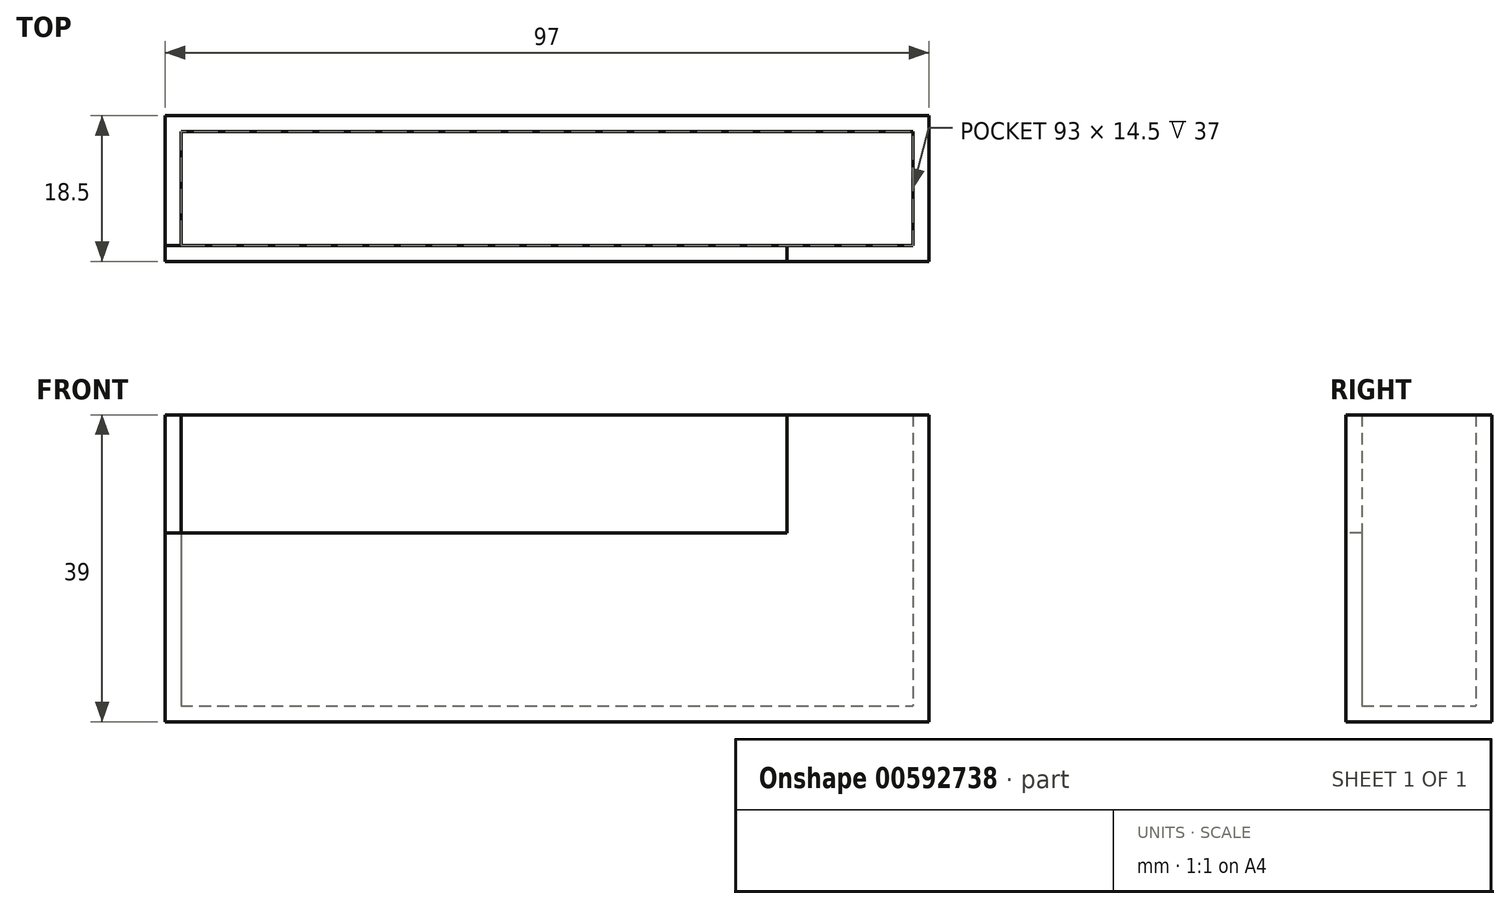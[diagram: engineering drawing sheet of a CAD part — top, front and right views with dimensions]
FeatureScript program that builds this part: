
annotation { "Feature Type Name" : "Feature", "Feature Type Description" : "" }
export const myFeature = defineFeature(function(context is Context, id is Id, definition is map)
    precondition{}
    {
        {
            var Q0;
            Q0=qCreatedBy(makeId("Top.planeOp"),FACE);
            var sketch = newSketch(context, id + "F0", { "sketchPlane" : qUnion([Q0])});
            skLineSegment(sketch, "E0.bottom", {"start": v(0, 0) * mm, "end": v(97, 0) * mm});
            skLineSegment(sketch, "E0.top", {"start": v(0, 18.5) * mm, "end": v(97, 18.5) * mm});
            skLineSegment(sketch, "E0.left", {"start": v(0, 0) * mm, "end": v(0, 18.5) * mm});
            skLineSegment(sketch, "E0.right", {"start": v(97, 0) * mm, "end": v(97, 18.5) * mm});
            skSolve(sketch);
        }
        {
            var Q0;
            Q0 = qSketchRegion(id + "F0", true);
            extrude(context, id + "F1", {"entities" : qUnion([Q0]), "depth" : 2 * mm, "offsetDistance" : 25 * mm});
        }
        {
            var Q0;
            Q0=makeQuery(id+"F1.opExtrude","CAP_FACE",FACE,{"disambiguationData":[OSD([sQuery(id+"F0.wireOp",EDGE,"E0.bottom"),sQuery(id+"F0.wireOp",EDGE,"E0.top"),sQuery(id+"F0.wireOp",EDGE,"E0.left"),sQuery(id+"F0.wireOp",EDGE,"E0.right")])],"isStart":false});
            var sketch = newSketch(context, id + "F2", { "sketchPlane" : qUnion([Q0])});
            skLineSegment(sketch, "E1.bottom", {"start": v(0, 0) * mm, "end": v(2, 0) * mm});
            skLineSegment(sketch, "E1.top", {"start": v(0, 2) * mm, "end": v(2, 2) * mm});
            skLineSegment(sketch, "E1.left", {"start": v(0, 0) * mm, "end": v(0, 2) * mm});
            skLineSegment(sketch, "E1.right", {"start": v(2, 0) * mm, "end": v(2, 2) * mm});
            skLineSegment(sketch, "E2.bottom", {"start": v(97, 18.5) * mm, "end": v(95, 18.5) * mm});
            skLineSegment(sketch, "E2.top", {"start": v(97, 16.5) * mm, "end": v(95, 16.5) * mm});
            skLineSegment(sketch, "E2.left", {"start": v(97, 18.5) * mm, "end": v(97, 16.5) * mm});
            skLineSegment(sketch, "E2.right", {"start": v(95, 18.5) * mm, "end": v(95, 16.5) * mm});
            skLineSegment(sketch, "E3.bottom", {"start": v(2, 2) * mm, "end": v(95, 2) * mm});
            skLineSegment(sketch, "E3.top", {"start": v(2, 16.5) * mm, "end": v(95, 16.5) * mm});
            skLineSegment(sketch, "E3.left", {"start": v(2, 2) * mm, "end": v(2, 16.5) * mm});
            skLineSegment(sketch, "E3.right", {"start": v(95, 2) * mm, "end": v(95, 16.5) * mm});
            skLineSegment(sketch, "E4.bottom", {"start": v(97, 18.5) * mm, "end": v(0, 18.5) * mm});
            skLineSegment(sketch, "E4.top", {"start": v(97, 0) * mm, "end": v(0, 0) * mm});
            skLineSegment(sketch, "E4.left", {"start": v(97, 18.5) * mm, "end": v(97, 0) * mm});
            skLineSegment(sketch, "E4.right", {"start": v(0, 18.5) * mm, "end": v(0, 0) * mm});
            skSolve(sketch);
        }
        {
            var Q0;
            Q0 = qSketchRegion(id + "F2", true);
            extrude(context, id + "F3", {"entities" : qUnion([Q0]), "operationType" : NewBodyOperationType.ADD, "depth" : 37 * mm, "offsetDistance" : 25 * mm});
        }
        {
            var Q0;
            Q0=makeQuery(id+"F3.boolean.opBoolean","MERGE",FACE,{"derivedFrom":[makeQuery(id+"F1.opExtrude","SWEPT_FACE",FACE,{"disambiguationData":[OSD([sQuery(id+"F0.wireOp",EDGE,"E0.bottom")])]}),makeQuery(id+"F3.opExtrude","SWEPT_FACE",FACE,{"disambiguationData":[OSD([sQuery(id+"F2.wireOp",EDGE,"E4.top")])]})]});
            var sketch = newSketch(context, id + "F4", { "sketchPlane" : qUnion([Q0])});
            skLineSegment(sketch, "E5.bottom", {"start": v(0, 39) * mm, "end": v(79, 39) * mm});
            skLineSegment(sketch, "E5.top", {"start": v(0, 24) * mm, "end": v(79, 24) * mm});
            skLineSegment(sketch, "E5.left", {"start": v(0, 39) * mm, "end": v(0, 24) * mm});
            skLineSegment(sketch, "E5.right", {"start": v(79, 39) * mm, "end": v(79, 24) * mm});
            skSolve(sketch);
        }
        {
            var Q0;
            Q0 = qSketchRegion(id + "F4", true);
            extrude(context, id + "F5", {"entities" : qUnion([Q0]), "operationType" : NewBodyOperationType.REMOVE, "oppositeDirection" : true, "depth" : 2 * mm, "offsetDistance" : 25 * mm});
        }
    });
